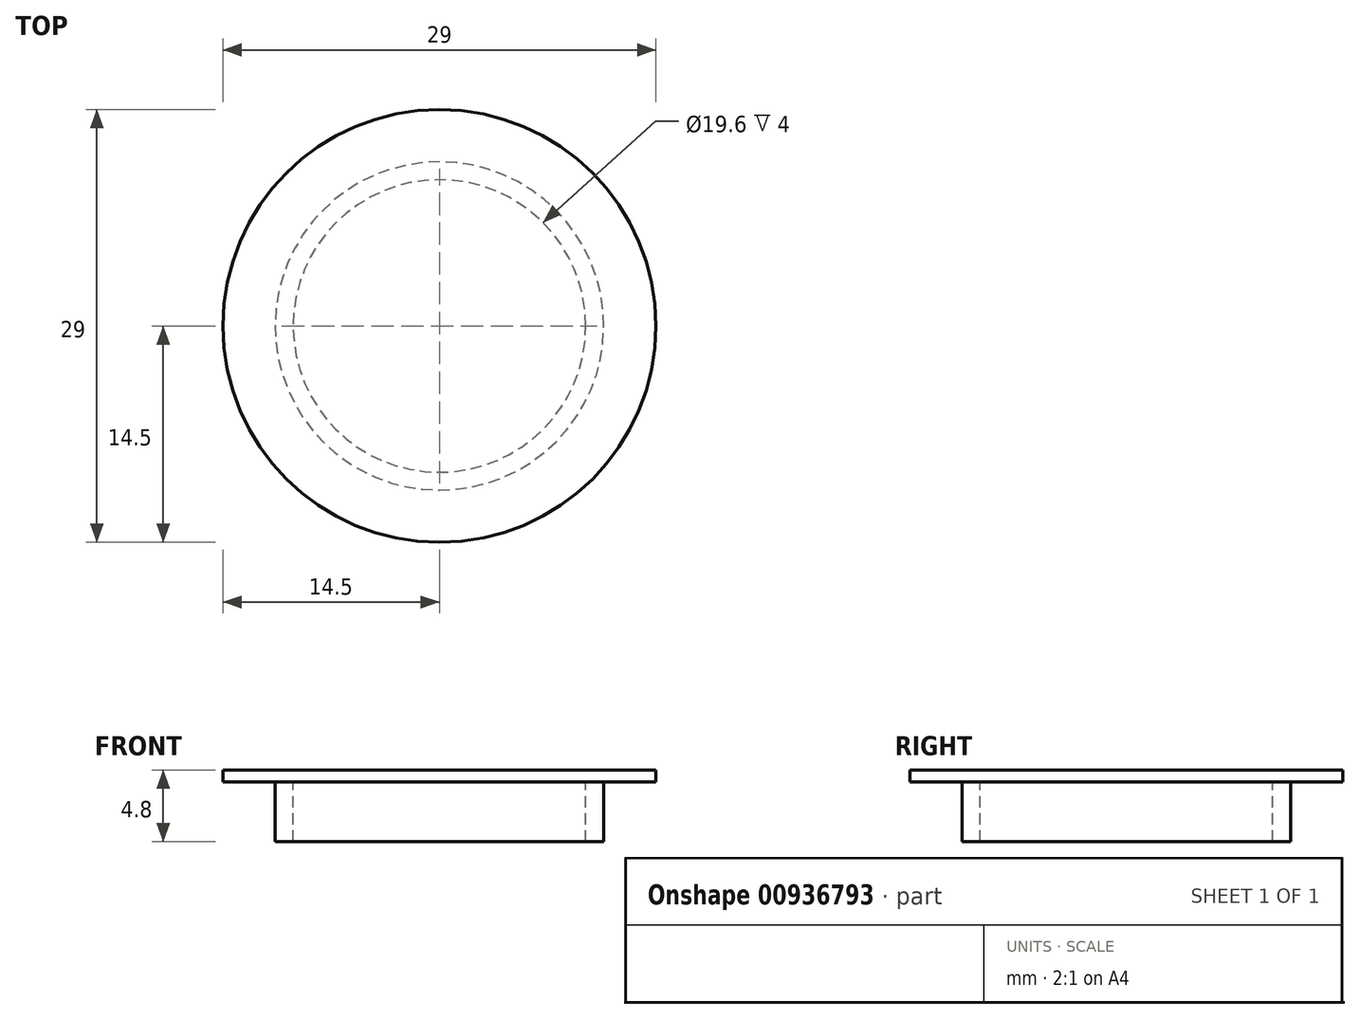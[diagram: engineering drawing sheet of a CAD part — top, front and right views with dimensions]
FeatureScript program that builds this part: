
annotation { "Feature Type Name" : "Feature", "Feature Type Description" : "" }
export const myFeature = defineFeature(function(context is Context, id is Id, definition is map)
    precondition{}
    {
        {
            var Q0;
            Q0=qCreatedBy(makeId("Top.planeOp"),FACE);
            var sketch = newSketch(context, id + "F0", { "sketchPlane" : qUnion([Q0])});
            skCircle(sketch, "E0", {"center": v(0, 0) * mm, "radius": 14.5 * mm});
            skCircle(sketch, "E1", {"center": v(0, 0) * mm, "radius": 11 * mm});
            skCircle(sketch, "E2", {"center": v(0, 0) * mm, "radius": 9.8 * mm});
            skSolve(sketch);
        }
        {
            var Q0;
            Q0 = qSketchRegion(id + "F0", true);
            var Q1;
            Q1=makeQuery(id+"F0.imprint","IMPRINT",FACE,{"disambiguationData":[TD([[makeQuery(id+"F0.imprint","IMPRINT",EDGE,{"derivedFrom":sQuery(id+"F0.wireOp",EDGE,"E1")}),1.0]])]});
            var Q2;
            Q2=makeQuery(id+"F0.imprint","IMPRINT",FACE,{"disambiguationData":[TD([[makeQuery(id+"F0.imprint","IMPRINT",EDGE,{"derivedFrom":sQuery(id+"F0.wireOp",EDGE,"E2")}),1.0]])]});
            extrude(context, id + "F1", {"entities" : qUnion([Q0, Q1, Q2]), "depth" : 0.8 * mm, "offsetDistance" : 25 * mm});
        }
        {
            var Q0;
            Q0=makeQuery(id+"F0.imprint","IMPRINT",FACE,{"disambiguationData":[TD([[makeQuery(id+"F0.imprint","IMPRINT",EDGE,{"derivedFrom":sQuery(id+"F0.wireOp",EDGE,"E1")}),1.0]])]});
            extrude(context, id + "F2", {"entities" : qUnion([Q0]), "operationType" : NewBodyOperationType.ADD, "oppositeDirection" : true, "depth" : 4 * mm, "offsetDistance" : 25 * mm});
        }
    });
